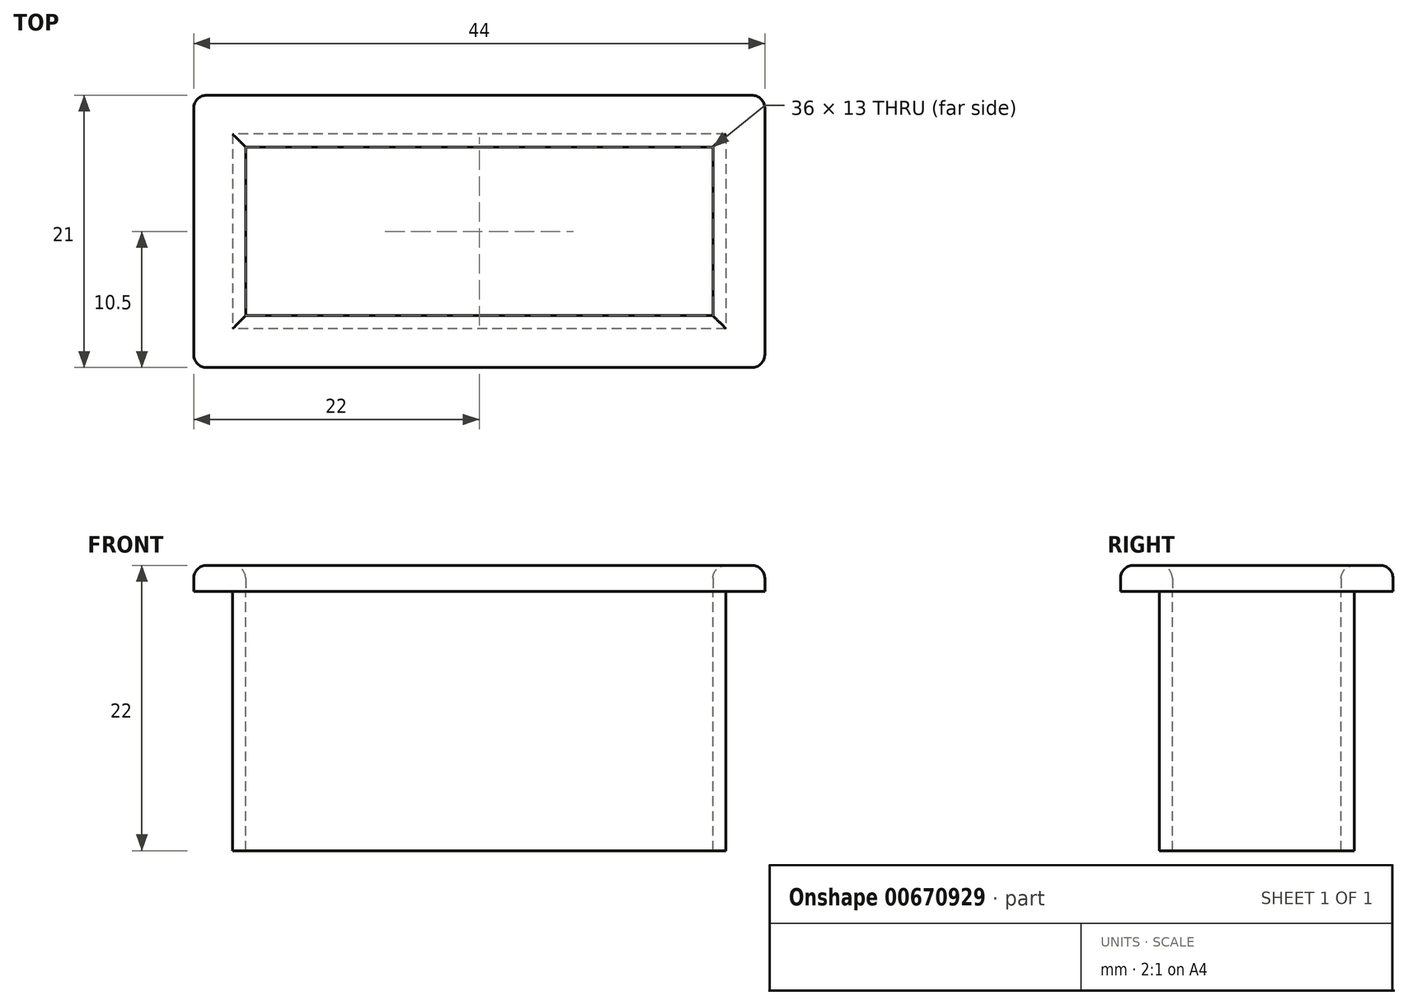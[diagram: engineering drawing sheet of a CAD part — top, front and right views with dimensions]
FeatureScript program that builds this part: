
annotation { "Feature Type Name" : "Feature", "Feature Type Description" : "" }
export const myFeature = defineFeature(function(context is Context, id is Id, definition is map)
    precondition{}
    {
        {
            var Q0;
            Q0=qCreatedBy(makeId("Top.planeOp"),FACE);
            var sketch = newSketch(context, id + "F0", { "sketchPlane" : qUnion([Q0])});
            skLineSegment(sketch, "E0.bottom", {"start": v(19, 7.5) * mm, "end": v(-19, 7.5) * mm});
            skLineSegment(sketch, "E0.top", {"start": v(19, -7.5) * mm, "end": v(-19, -7.5) * mm});
            skLineSegment(sketch, "E0.left", {"start": v(19, 7.5) * mm, "end": v(19, -7.5) * mm});
            skLineSegment(sketch, "E0.right", {"start": v(-19, 7.5) * mm, "end": v(-19, -7.5) * mm});
            skPoint(sketch, "E0.middle", {"position": v(0, 0) * mm});
            skLineSegment(sketch, "E1.0", {"start": v(22, 10.5) * mm, "end": v(-22, 10.5) * mm});
            skLineSegment(sketch, "E1.1", {"start": v(22, 10.5) * mm, "end": v(22, -10.5) * mm});
            skLineSegment(sketch, "E1.2", {"start": v(22, -10.5) * mm, "end": v(-22, -10.5) * mm});
            skLineSegment(sketch, "E1.3", {"start": v(-22, 10.5) * mm, "end": v(-22, -10.5) * mm});
            skLineSegment(sketch, "E2.0", {"start": v(18, 6.5) * mm, "end": v(18, -6.5) * mm});
            skLineSegment(sketch, "E2.1", {"start": v(18, 6.5) * mm, "end": v(-18, 6.5) * mm});
            skLineSegment(sketch, "E2.2", {"start": v(-18, 6.5) * mm, "end": v(-18, -6.5) * mm});
            skLineSegment(sketch, "E2.3", {"start": v(18, -6.5) * mm, "end": v(-18, -6.5) * mm});
            skSolve(sketch);
        }
        {
            var Q0;
            Q0=makeQuery(id+"F0.imprint","IMPRINT",FACE,{"disambiguationData":[TD([[makeQuery(id+"F0.imprint","IMPRINT",EDGE,{"derivedFrom":sQuery(id+"F0.wireOp",EDGE,"E0.bottom")}),1.0]])]});
            extrude(context, id + "F1", {"entities" : qUnion([Q0]), "oppositeDirection" : true, "depth" : 20 * mm, "offsetDistance" : 25 * mm});
        }
        {
            var Q0;
            Q0=makeQuery(id+"F0.imprint","IMPRINT",FACE,{"disambiguationData":[TD([[makeQuery(id+"F0.imprint","IMPRINT",EDGE,{"derivedFrom":sQuery(id+"F0.wireOp",EDGE,"E0.bottom")}),-1.0]])]});
            var Q1;
            Q1=makeQuery(id+"F0.imprint","IMPRINT",FACE,{"disambiguationData":[TD([[makeQuery(id+"F0.imprint","IMPRINT",EDGE,{"derivedFrom":sQuery(id+"F0.wireOp",EDGE,"E0.bottom")}),1.0]])]});
            extrude(context, id + "F2", {"entities" : qUnion([Q0, Q1]), "depth" : 2 * mm, "offsetDistance" : 25 * mm});
        }
        {
            var Q0;
            Q0=makeQuery(id+"F2.opExtrude","CAP_EDGE",EDGE,{"disambiguationData":[OSD([sQuery(id+"F0.wireOp",EDGE,"E2.1")])],"isStart":false});
            var Q1;
            Q1=makeQuery(id+"F2.opExtrude","CAP_EDGE",EDGE,{"disambiguationData":[OSD([sQuery(id+"F0.wireOp",EDGE,"E2.2")])],"isStart":false});
            var Q2;
            Q2=makeQuery(id+"F2.opExtrude","CAP_EDGE",EDGE,{"disambiguationData":[OSD([sQuery(id+"F0.wireOp",EDGE,"E2.3")])],"isStart":false});
            var Q3;
            Q3=makeQuery(id+"F2.opExtrude","CAP_EDGE",EDGE,{"disambiguationData":[OSD([sQuery(id+"F0.wireOp",EDGE,"E2.0")])],"isStart":false});
            var Q4;
            Q4=makeQuery(id+"F2.opExtrude","CAP_EDGE",EDGE,{"disambiguationData":[OSD([sQuery(id+"F0.wireOp",EDGE,"E1.3")])],"isStart":false});
            var Q5;
            Q5=makeQuery(id+"F2.opExtrude","CAP_EDGE",EDGE,{"disambiguationData":[OSD([sQuery(id+"F0.wireOp",EDGE,"E1.0")])],"isStart":false});
            var Q6;
            Q6=makeQuery(id+"F2.opExtrude","CAP_EDGE",EDGE,{"disambiguationData":[OSD([sQuery(id+"F0.wireOp",EDGE,"E1.2")])],"isStart":false});
            var Q7;
            Q7=makeQuery(id+"F2.opExtrude","CAP_EDGE",EDGE,{"disambiguationData":[OSD([sQuery(id+"F0.wireOp",EDGE,"E1.1")])],"isStart":false});
            var Q8;
            Q8=makeQuery(id+"F2.opExtrude","SWEPT_EDGE",EDGE,{"disambiguationData":[OSD([sQuery(id+"F0.wireOp",EDGE,"E1.2"),sQuery(id+"F0.wireOp",EDGE,"E1.3")])]});
            var Q9;
            Q9=makeQuery(id+"F2.opExtrude","SWEPT_EDGE",EDGE,{"disambiguationData":[OSD([sQuery(id+"F0.wireOp",EDGE,"E1.1"),sQuery(id+"F0.wireOp",EDGE,"E1.2")])]});
            var Q10;
            Q10=makeQuery(id+"F2.opExtrude","SWEPT_EDGE",EDGE,{"disambiguationData":[OSD([sQuery(id+"F0.wireOp",EDGE,"E1.0"),sQuery(id+"F0.wireOp",EDGE,"E1.1")])]});
            var Q11;
            Q11=makeQuery(id+"F2.opExtrude","SWEPT_EDGE",EDGE,{"disambiguationData":[OSD([sQuery(id+"F0.wireOp",EDGE,"E1.0"),sQuery(id+"F0.wireOp",EDGE,"E1.3")])]});
            fillet(context, id + "F3", {"entities" : qUnion([Q0, Q1, Q2, Q3, Q4, Q5, Q6, Q7, Q8, Q9, Q10, Q11]), "radius" : 1 * mm, "tangentPropagation" : true, "allowEdgeOverflow" : false});
        }
    });
